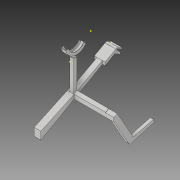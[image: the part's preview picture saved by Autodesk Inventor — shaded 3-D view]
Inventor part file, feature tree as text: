
AUTODESK INVENTOR PART (.ipt)
format: ipt  version: 2017 (Build 210142000, 142)  size: 576,000 bytes
history: native  units: mm
features: thicken_offset x49, sketch x39, extrude x32, plane x6, projected_geometry x3, mirror x1
ambient origin geometry x8: Origin, YZ Plane, XZ Plane, XY Plane, X Axis, Y Axis, Z Axis, Center Point
bodies: Solid1 (feature_tree)
feature tree (130):
  extrude  "Extrusion1"  Depth=10.0mm TaperAngle=0.0deg
  thicken_offset  "Thicken1"
  thicken_offset  "Thicken2"
  thicken_offset  "Thicken3"
  thicken_offset  "Thicken4"
  extrude  "Extrusion2"  Depth=5.0mm
  extrude  "Extrusion3"  Depth=5.0mm
  thicken_offset  "Thicken5"
  extrude  "Extrusion4"  Depth=200.0mm
  thicken_offset  "Thicken6"
  thicken_offset  "Thicken7"
  plane  "Work Plane1"
  extrude  "Extrusion6"  Depth=30.0mm
  thicken_offset  "Thicken8"
  thicken_offset  "Thicken9"
  thicken_offset  "Thicken10"
  extrude  "Extrusion7"  Depth=40.0mm TaperAngle=0.0deg
  thicken_offset  "Thicken12"
  extrude  "Extrusion8"  Depth=100.0mm
  extrude  "Extrusion9"  Depth=40.0mm
  thicken_offset  "Thicken13"
  thicken_offset  "Thicken14"
  extrude  "Extrusion10"  Depth=40.0mm
  sketch  "Sketch11"  dims[d25=5.0mm d26=-40.0mm]
  extrude  "Extrusion11"  [1 undecoded]
  thicken_offset  "Thicken15"
  thicken_offset  "Thicken16"
  thicken_offset  "Thicken17"
  thicken_offset  "Thicken18"
  plane  "Work Plane2"
  extrude  "Extrusion12"  Depth=40.0mm
  thicken_offset  "Thicken19"
  thicken_offset  "Thicken20"
  extrude  "Extrusion13"  Depth=20.0mm
  thicken_offset  "Thicken21"
  extrude  "Extrusion14"  Depth=20.0mm
  sketch  "Sketch16"  dims[d39=65.0mm d40=65.0mm]
  plane  "Work Plane3"
  extrude  "Extrusion15"  Depth=20.0mm TaperAngle=0.0deg
  sketch  "Sketch18"  dims[d45=15.0mm d46=15.0mm]
  plane  "Work Plane4"
  extrude  "Extrusion16"  Depth=65.0mm
  thicken_offset  "Thicken22"
  thicken_offset  "Thicken23"
  thicken_offset  "Thicken24"
  thicken_offset  "Thicken25"
  extrude  "Extrusion17"  Depth=70.0mm TaperAngle=0.0deg
  extrude  "Extrusion18"  Depth=15.0mm
  thicken_offset  "Thicken26"
  thicken_offset  "Thicken27"
  sketch  "Sketch22"  dims[d55=2.0mm d56=2.0mm]
  extrude  "Extrusion19"  Depth=7.0mm
  sketch  "Sketch24"  dims[d59=4.0mm d60=2.0mm]
  plane  "Work Plane5"
  extrude  "Extrusion20"  Depth=70.0mm TaperAngle=0.0deg
  extrude  "Extrusion21"  Depth=70.0mm
  extrude  "Extrusion22"  Depth=2.0mm
  extrude  "Extrusion23"  Depth=4.0mm
  thicken_offset  "Thicken28"
  extrude  "Extrusion24"  Depth=2.0mm
  thicken_offset  "Thicken29"
  extrude  "Extrusion25"  [1 undecoded]
  extrude  "Extrusion26"  Depth=30.0mm
  thicken_offset  "Thicken30"
  thicken_offset  "Thicken31"
  plane  "Work Plane6"
  mirror  "Mirror1"
  extrude  "Extrusion27"  Depth=20.0mm
  extrude  "Extrusion28"  Depth=70.0mm TaperAngle=0.0deg
  sketch  "Sketch34"  dims[d84=150.0mm]
  sketch  "Sketch35"  dims[d85=150.0mm]
  extrude  "Extrusion29"  Depth=30.0mm
  extrude  "Extrusion30"  [1 undecoded]
  extrude  "Extrusion31"  [1 undecoded]
  extrude  "Extrusion32"  Depth=150.0mm
  thicken_offset  "Thicken32"
  thicken_offset  "Thicken33"
  thicken_offset  "Thicken34"
  thicken_offset  "Thicken35"
  thicken_offset  "Thicken36"
  thicken_offset  "Thicken37"
  thicken_offset  "Thicken38"
  thicken_offset  "Thicken39"
  extrude  "Extrusion33"  Depth=150.0mm
  thicken_offset  "Thicken40"
  thicken_offset  "Thicken41"
  thicken_offset  "Thicken42"
  thicken_offset  "Thicken43"
  thicken_offset  "Thicken44"
  thicken_offset  "Thicken45"
  thicken_offset  "Thicken46"
  thicken_offset  "Thicken47"
  thicken_offset  "Thicken48"
  thicken_offset  "Thicken49"
  thicken_offset  "Thicken50"
  sketch  "Sketch1"  dims[d1=18.0mm d2=10.0mm d3=0.0mm]
  sketch  "Sketch2"  dims[d4=5.0mm d5=5.0mm]
  sketch  "Sketch3"  dims[d6=5.0mm d7=5.0mm]
  sketch  "Sketch4"  dims[d8=200.0mm d9=200.0mm]
  sketch  "Sketch6"  dims[d10=30.0mm d11=30.0mm]
  sketch  "Sketch7"  dims[d12=100.0mm d13=0.0mm d14=40.0mm d15=0.0mm]
  sketch  "Sketch8"  dims[d16=100.0mm d17=100.0mm]
  sketch  "Sketch9"  dims[d18=40.0mm d19=0.0mm d20=40.0mm]
  sketch  "Sketch10"  dims[d21=40.0mm d24=5.0mm]
  sketch  "Sketch12"  dims[d27=40.0mm d28=0.0mm d29=100.0mm]
  sketch  "Sketch13"  dims[d30=100.0mm d31=20.0mm]
  sketch  "Sketch14"  dims[d32=20.0mm d33=20.0mm]
  sketch  "Sketch15"  dims[d34=20.0mm d35=400.0mm d36=0.0mm]
  sketch  "Sketch17"  dims[d41=300.0mm d42=0.0mm d43=70.0mm d44=0.0mm]
  sketch  "Sketch19"  dims[d47=7.0mm d48=7.0mm]
  sketch  "Sketch20"  dims[d49=35.0mm d50=70.0mm d51=0.0mm]
  projected_geometry  "Projected Loop1"
  sketch  "Sketch21"  dims[d52=70.0mm d53=0.0mm d54=2.0mm]
  sketch  "Sketch23"  dims[d57=2.0mm d58=4.0mm]
  sketch  "Sketch25"  dims[d61=2.0mm d62=-167.5mm]
  sketch  "Sketch26"  dims[d63=30.0mm d64=0.0mm d65=150.0mm]
  projected_geometry  "Projected Loop2"
  sketch  "Sketch27"  dims[d66=150.0mm d67=20.0mm]
  projected_geometry  "Projected Loop3"
  sketch  "Sketch28"  dims[d68=20.0mm d69=70.0mm d70=0.0mm]
  sketch  "Sketch29"  dims[d71=30.0mm d72=30.0mm]
  sketch  "Sketch30"  dims[d73=30.0mm d74=0.0mm d75=-15.0mm]
  sketch  "Sketch31"  dims[d76=14.0mm d77=0.0mm d78=-2.0mm]
  sketch  "Sketch32"  dims[d79=14.0mm d80=0.0mm d81=150.0mm]
  sketch  "Sketch33"  dims[d82=150.0mm d83=150.0mm]
  sketch  "Sketch36"  dims[d86=150.0mm]
  sketch  "Sketch37"  dims[d87=150.0mm]
  sketch  "Sketch38"  dims[d88=150.0mm]
  sketch  "Sketch39"  dims[d89=40.0mm d90=0.0mm]
  sketch  "Sketch40"  dims[d91=40.0mm d92=0.0mm d93=3.0mm d94=3.0mm d95=3.0mm d96=3.0mm d97=50.0mm d98=0.0mm d99=-2.0mm d100=31.0mm d101=0.0mm d102=400.0mm d103=0.0mm d104=200.0mm d105=0.0mm d106=200.0mm d107=0.0mm d108=20.0mm d109=20.0mm d110=30.0mm d111=0.0mm d112=40.0mm d113=40.0mm d114=30.0mm d115=0.0mm d116=30.0mm d117=0.0mm d118=2.0mm d119=2.0mm d120=40.0mm d121=40.0mm d122=-20.0mm d123=267.0mm d124=30.0mm d125=0.0mm d126=28.0mm d127=196.0mm d128=0.0mm d129=25.0mm d130=0.0mm d131=45.0mm d132=0.0mm d133=28.0mm d134=0.0mm d135=580.0mm d136=0.0mm d137=10.0mm d138=10.0mm d139=10.0mm d140=10.0mm d141=10.0mm d142=10.0mm d143=10.0mm d144=10.0mm d145=20.0mm d146=20.0mm d147=20.0mm d148=20.0mm d149=20.0mm d150=20.0mm d151=20.0mm d152=20.0mm d153=28.0mm d154=0.0mm d155=20.0mm d156=20.0mm d157=20.0mm d158=20.0mm d159=5.0mm d160=5.0mm d161=5.0mm d162=5.0mm d163=5.0mm d164=5.0mm d165=5.0mm d166=5.0mm d167=30.0mm d168=30.0mm d169=5.0mm d170=5.0mm d171=3.0mm d172=3.0mm d173=3.0mm d174=3.0mm d175=10.0mm d176=10.0mm]
note: 4 required parameter values undecoded (feature->parameter linkage not recoverable at this tier; creation-order binding heuristic only, values carry confidence <= 0.55)
